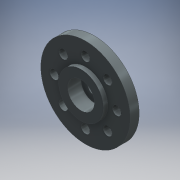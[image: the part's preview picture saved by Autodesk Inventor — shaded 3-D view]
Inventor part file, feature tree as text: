
AUTODESK INVENTOR PART (.ipt)
format: ipt  version: 2016 (Build 200138000, 138)  size: 160,256 bytes
history: native  units: mm
features: extrude x6, sketch x5, other x1
ambient origin geometry x8: Origin, YZ Plane, XZ Plane, XY Plane, X Axis, Y Axis, Z Axis, Center Point
bodies: Body1 (feature_tree)
feature tree (12):
  other  "ソリッド1"
  extrude  "押し出し1"  Depth=20.0mm
  extrude  "押し出し2"  Depth=2.0mm TaperAngle=0.0deg
  extrude  "押し出し3"  Depth=14.0mm
  extrude  "押し出し4"  Depth=2.0mm
  extrude  "押し出し5"  Depth=2.0mm
  extrude  "押し出し6"  Depth=2.0mm
  sketch  "スケッチ2"
  sketch  "スケッチ3"
  sketch  "スケッチ4"
  sketch  "スケッチ5"
  sketch  "スケッチ6"
